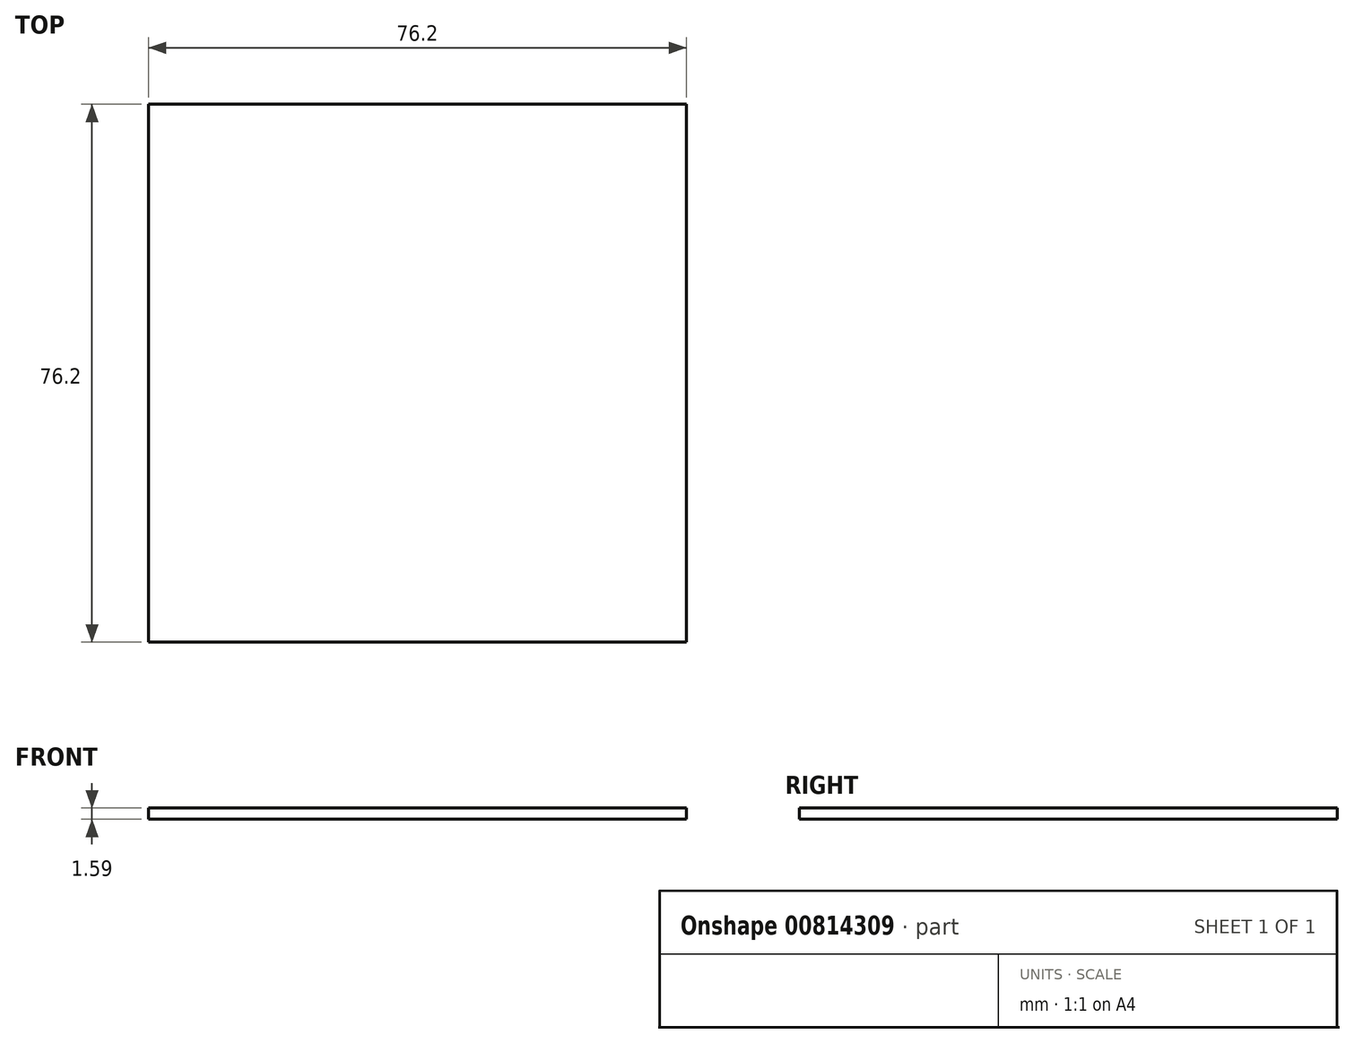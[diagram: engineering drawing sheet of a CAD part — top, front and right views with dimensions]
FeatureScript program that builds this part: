
annotation { "Feature Type Name" : "Feature", "Feature Type Description" : "" }
export const myFeature = defineFeature(function(context is Context, id is Id, definition is map)
    precondition{}
    {
        {
            var Q0;
            Q0=qCreatedBy(makeId("Top.planeOp"),FACE);
            var sketch = newSketch(context, id + "F0", { "sketchPlane" : qUnion([Q0])});
            skLineSegment(sketch, "E0", {"start": v(38.1, 0) * mm, "end": v(38.1, 38.1) * mm});
            skLineSegment(sketch, "E1", {"start": v(38.1, 38.1) * mm, "end": v(-38.1, 38.1) * mm});
            skLineSegment(sketch, "E2", {"start": v(-38.1, 38.1) * mm, "end": v(-38.1, -38.1) * mm});
            skLineSegment(sketch, "E3", {"start": v(-38.1, -38.1) * mm, "end": v(38.1, -38.1) * mm});
            skLineSegment(sketch, "E4", {"start": v(38.1, -38.1) * mm, "end": v(38.1, 0) * mm});
            skSolve(sketch);
        }
        {
            var Q0;
            Q0=makeQuery(id+"F0.imprint","IMPRINT",FACE,{"disambiguationData":[TD([[makeQuery(id+"F0.imprint","IMPRINT",EDGE,{"derivedFrom":sQuery(id+"F0.wireOp",EDGE,"E0")}),1.0]])]});
            extrude(context, id + "F1", {"entities" : qUnion([Q0]), "depth" : 1.59 * mm, "offsetDistance" : 25.4 * mm});
        }
    });
